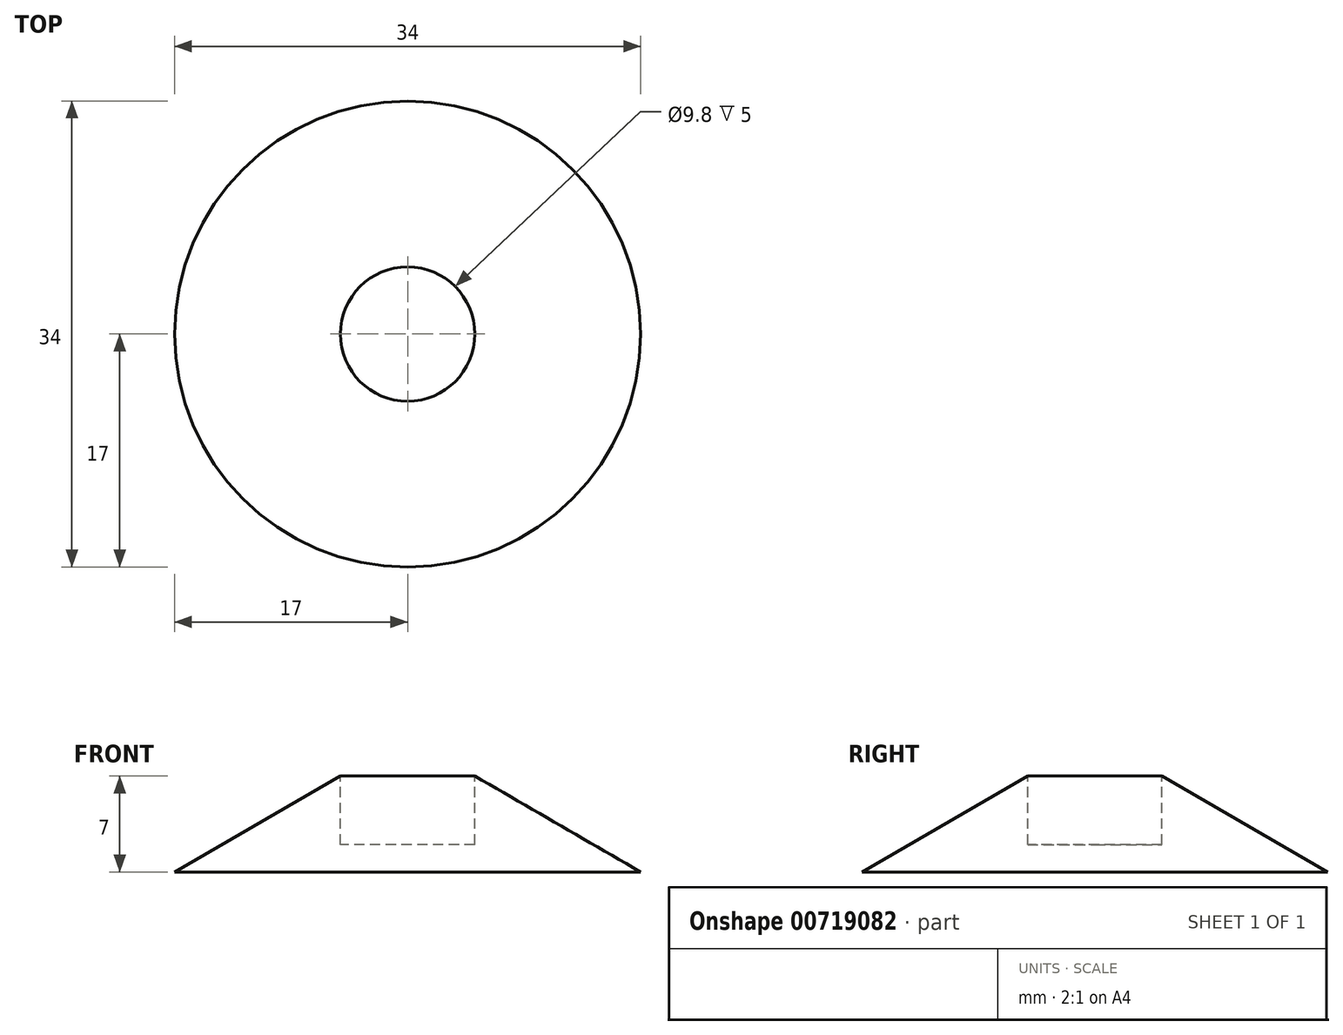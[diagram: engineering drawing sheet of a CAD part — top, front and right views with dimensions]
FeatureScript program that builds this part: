
annotation { "Feature Type Name" : "Feature", "Feature Type Description" : "" }
export const myFeature = defineFeature(function(context is Context, id is Id, definition is map)
    precondition{}
    {
        {
            var Q0;
            Q0=qCreatedBy(makeId("Front.planeOp"),FACE);
            var sketch = newSketch(context, id + "F0", { "sketchPlane" : qUnion([Q0])});
            skLineSegment(sketch, "E0", {"start": v(-17, 0) * mm, "end": v(-4.9, 7) * mm});
            skLineSegment(sketch, "E1", {"start": v(-4.9, 7) * mm, "end": v(-4.9, 2) * mm});
            skLineSegment(sketch, "E2", {"start": v(-4.9, 2) * mm, "end": v(0, 2) * mm});
            skLineSegment(sketch, "E3", {"start": v(0, 2) * mm, "end": v(0, 0) * mm});
            skLineSegment(sketch, "E4", {"start": v(0, 0) * mm, "end": v(-17, 0) * mm});
            skSolve(sketch);
        }
        {
            var Q0;
            Q0=makeQuery(id+"F0.imprint","IMPRINT",FACE,{"disambiguationData":[TD([[makeQuery(id+"F0.imprint","IMPRINT",EDGE,{"derivedFrom":sQuery(id+"F0.wireOp",EDGE,"E0")}),-1.0]])]});
            var Q1;
            Q1=sQuery(id+"F0.wireOp",EDGE,"E3");
            revolve(context, id + "F1", {"surfaceOperationType" : NewSurfaceOperationType.NEW, "entities" : qUnion([Q0]), "axis" : qUnion([Q1]), "revolveType" : RevolveType.FULL});
        }
    });
